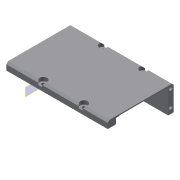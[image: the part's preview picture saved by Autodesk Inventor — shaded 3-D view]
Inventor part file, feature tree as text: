
AUTODESK INVENTOR PART (.ipt)
format: ipt  version: 2019 (Build 230136000, 136)  size: 336,384 bytes
history: native  units: mm
features: reference x31, sketch x7, extrude x7, other x6, plane x5, projected_geometry x5, chamfer x4, hole x1
ambient origin geometry x8: Origin, YZ Plane, XZ Plane, XY Plane, X Axis, Y Axis, Z Axis, Center Point
bodies: Body1 (feature_tree)
feature tree (66):
  plane  "Arbeitsebene6"
  sketch  "Skizze6"  dims[d39=1.0mm d41=13.9mm]
  plane  "Arbeitsebene7"
  extrude  "Extrusion6"  Depth=13.9mm
  extrude  "Extrusion7"  Depth=2.0mm TaperAngle=0.0deg
  plane  "Arbeitsebene8"
  extrude  "Extrusion8"  Depth=4.3mm
  hole  "Bohrung1"  [1 undecoded]
  chamfer  "Fase1"  Distance=2.0mm
  chamfer  "Fase2"  Distance=1.0mm
  extrude  "Extrusion10"  Depth=2.0mm
  sketch  "Skizze12"  dims[d54=8.9mm]
  plane  "Arbeitsebene9"
  extrude  "Extrusion11"  Depth=2.0mm
  extrude  "Extrusion12"  Depth=0.4mm
  extrude  "Extrusion14"  Depth=50.0mm TaperAngle=0.0deg
  chamfer  "Fase4"  Distance=1.75mm
  plane  "Arbeitsebene10"
  chamfer  "Fase5"  Distance=11.0mm
  reference  "Referenz13"
  reference  "Referenz14"
  reference  "Referenz15"
  reference  "Referenz16"
  reference  "Referenz17"
  reference  "Referenz18"
  reference  "Referenz19"
  reference  "Referenz20"
  reference  "Referenz21"
  reference  "Referenz22"
  reference  "Referenz23"
  sketch  "Skizze7"  dims[d42=0.1mm d43=2.0mm d44=0.0mm]
  projected_geometry  "Projizierte Kontur5"
  reference  "Referenz24"
  reference  "Referenz25"
  reference  "Referenz26"
  reference  "Referenz27"
  reference  "Referenz28"
  reference  "Referenz29"
  reference  "Referenz30"
  reference  "Referenz31"
  projected_geometry  "Projizierte Kontur6"
  reference  "Referenz32"
  reference  "Referenz33"
  sketch  "Skizze9"  dims[d48=4.3mm d50=9.0mm]
  projected_geometry  "Projizierte Kontur7"
  sketch  "Skizze11"  dims[d51=17.4mm d52=17.9mm d53=3.9mm]
  projected_geometry  "Projizierte Kontur8"
  sketch  "Skizze13"  dims[d55=17.9mm d56=2.0mm d57=0.0mm]
  sketch  "Skizze15"  dims[d58=8.9mm d60=1.0mm d61=0.5mm d63=0.5mm d65=0.4mm d72=50.0mm d73=0.0mm d74=1.75mm d75=11.0mm d76=11.0mm d77=11.0mm d78=1.8mm d79=6.0mm d80=4.0mm d81=2.0mm d82=90.0deg d83=12.0mm d84=20.594885mm d87=1.0mm d88=2.0mm d89=45.0deg d90=1.0mm d91=2.0mm d92=45.0deg d93=2.8mm d94=10.0mm d95=0.0mm d96=13.0mm d97=0.0mm d101=1.8mm d102=1.8mm d103=8.0mm d104=0.0mm d113=36.0mm d116=8.0mm d117=8.0mm d118=3.0mm d119=0.0mm d120=5.5mm d122=5.5mm d126=3.0mm d127=2.0mm d128=45.0deg d132=0.0mm d133=3.0mm d134=0.75mm d135=0.75mm d136=0.6mm d137=1.0mm d138=2.0mm d139=45.0deg d140=1.75mm d141=8.4mm]
  projected_geometry  "Projizierte Kontur11"
  reference  "Referenz38"
  reference  "Referenz39"
  reference  "Referenz40"
  reference  "Referenz41"
  reference  "Referenz42"
  reference  "Referenz43"
  reference  "Referenz44"
  reference  "Referenz45"
  reference  "Referenz46"
  reference  "Referenz47"
  other  "<userpath>\Documents\Inventor\HITscope\HITscope_v0.iam"
  other  "HITscope_v0.iam"
  other  "00_ESP32_Board:1"
  other  "<userpath>\Documents\Inventor\HITscope\Assembly_HITscope.iam"
  other  "Assembly_HITscope.iam"
  other  "HITscope_v0:1"
note: 1 required parameter value undecoded (feature->parameter linkage not recoverable at this tier; creation-order binding heuristic only, values carry confidence <= 0.55)
